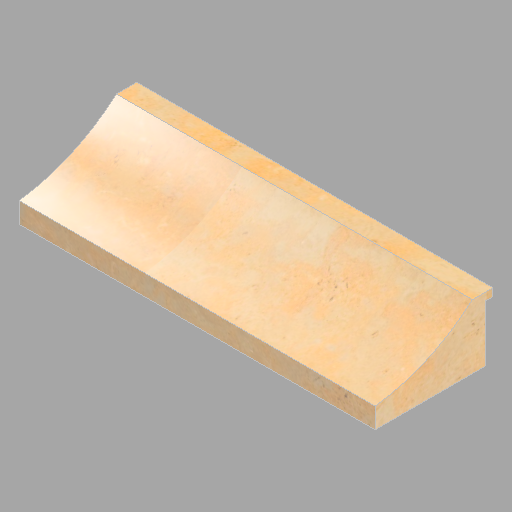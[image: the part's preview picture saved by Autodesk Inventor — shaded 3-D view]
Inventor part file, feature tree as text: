
AUTODESK INVENTOR PART (.ipt)
format: ipt  version: 2022.2 (Build 262287010, 287A)  size: 273,920 bytes
history: native  units: in
note: dims shown in document units (in); Inventor stores cm internally (conversion verified against a paired STEP export)
features: revolve x2, other x1, direct_edit x1
ambient origin geometry x8: Origin, YZ Plane, XZ Plane, XY Plane, X Axis, Y Axis, Z Axis, Center Point
bodies: Solid1 (feature_tree)
feature tree (4):
  other  "North (9)"
  direct_edit  "Direct Edit1"
  revolve  "Rotate1"  [1 undecoded]
  revolve  "Rotate2"  Angle=90.0deg
note: 1 required parameter value undecoded (feature->parameter linkage not recoverable at this tier; creation-order binding heuristic only, values carry confidence <= 0.55)
